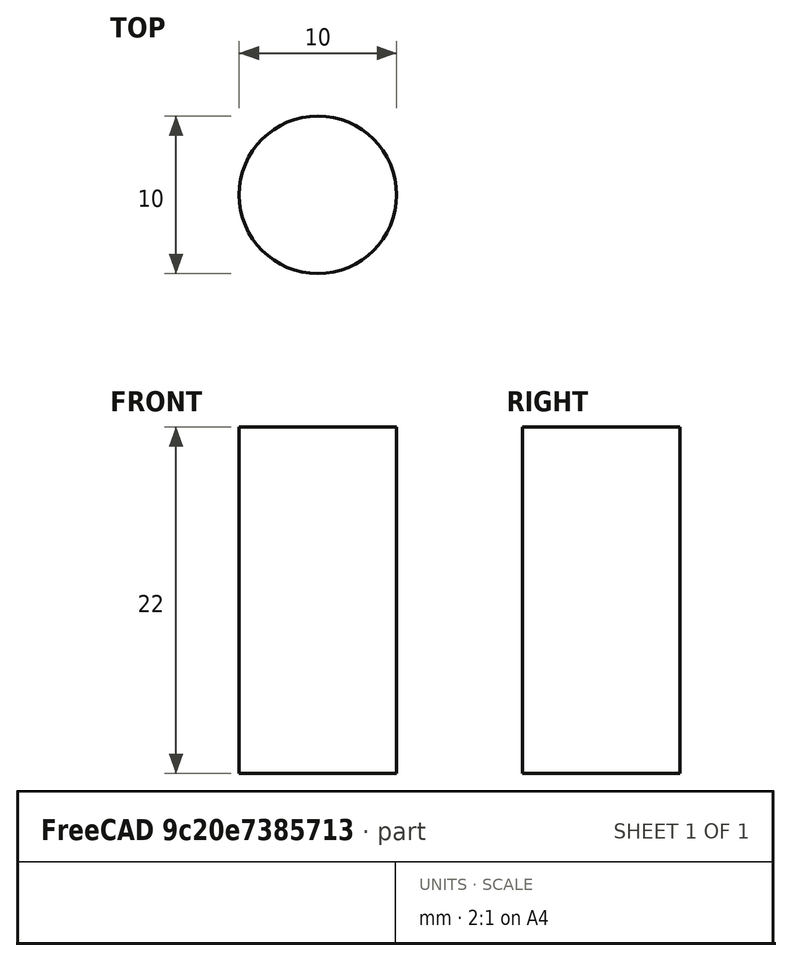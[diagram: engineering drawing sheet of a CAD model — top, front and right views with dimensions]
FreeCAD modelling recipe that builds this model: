
FCSTD DOCUMENT  (FreeCAD 0.21R33668 +26 (Git))
Label: dowel
License: All rights reserved
LicenseURL: https://en.wikipedia.org/wiki/All_rights_reserved
objects: Sketcher::SketchObject×1, PartDesign::Pad×1, PartDesign::Body×1, App::Part×1
note: 4 computed .brp shape members not serialized (recipe doc carries the construction recipe); baked Part::Feature solids carry a one-line shape summary decoded from their .brp

FEATURE [Sketcher::SketchObject] Sketch003
  FullyConstrained = true
  MapMode = 5
  Support = -> [XY_Plane005]
  sketch-geometry (1):
    g0: Circle CenterX=50 CenterY=0 CenterZ=0 NormalX=0 NormalY=0 NormalZ=1 AngleXU=0 Radius=5
  constraints (3):
    c: PointOnObject(g0,g-1)
    c: Diameter(g0) = 10
    c: DistanceX(g0) = 50
FEATURE [PartDesign::Pad] Pad002
  Direction = (0,0,1)
  Length = 22
  Length2 = 10
  Midplane = true
  Profile = -> Sketch003
  ReferenceAxis = -> Sketch003 [N_Axis]
  Type = 0
FEATURE [PartDesign::Body] Body002  label="Body"
  Group = -> [Sketch003,Pad002]
  Origin = -> Origin005
  Tip = -> Pad002
FEATURE [App::Part] Part002  label="Part"
  Group = -> [Body002]
  Origin = -> Origin004
